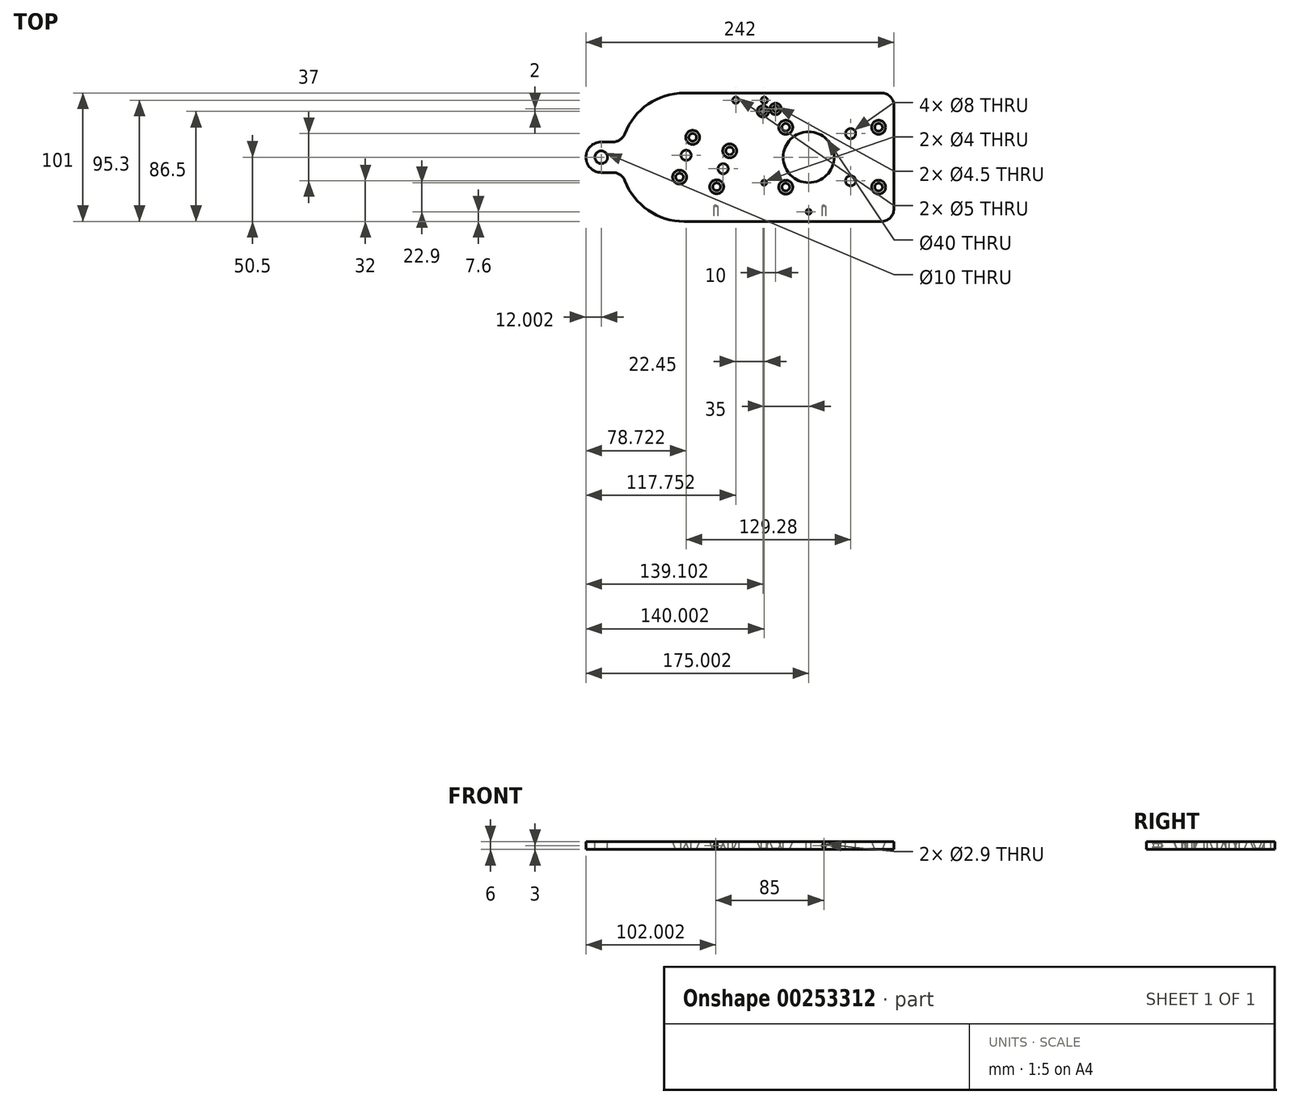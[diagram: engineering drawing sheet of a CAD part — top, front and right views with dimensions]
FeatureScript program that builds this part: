
annotation { "Feature Type Name" : "Feature", "Feature Type Description" : "" }
export const myFeature = defineFeature(function(context is Context, id is Id, definition is map)
    precondition{}
    {
        {
            var Q0;
            Q0=qCreatedBy(makeId("Top.planeOp"),FACE);
            var sketch = newSketch(context, id + "F0", { "sketchPlane" : qUnion([Q0])});
            skLineSegment(sketch, "E0.bottom", {"start": v(82.4, 50.5) * mm, "end": v(-82.4, 50.5) * mm});
            skLineSegment(sketch, "E0.top", {"start": v(82.4, -50.5) * mm, "end": v(-82.4, -50.5) * mm});
            skLineSegment(sketch, "E0.left", {"start": v(82.4, 50.5) * mm, "end": v(82.4, -50.5) * mm});
            skPoint(sketch, "E0.middle", {"position": v(0, 0) * mm});
            skLineSegment(sketch, "E1", {"start": v(-138.4, 12) * mm, "end": v(-147.6, 12) * mm});
            skLineSegment(sketch, "E2", {"start": v(-147.6, -12) * mm, "end": v(-138.4, -12) * mm});
            skCircle(sketch, "E3", {"center": v(-147.6, 0) * mm, "radius": 5 * mm});
            skCircle(sketch, "E4", {"center": v(15.4, 0) * mm, "radius": 20 * mm});
            skCircle(sketch, "E5", {"center": v(-80.89, 1.52) * mm, "radius": 4 * mm});
            skCircle(sketch, "E6", {"center": v(-51.76, -9.1) * mm, "radius": 4 * mm});
            skCircle(sketch, "E7", {"center": v(48.4, 18.5) * mm, "radius": 4 * mm});
            skCircle(sketch, "E8", {"center": v(48.4, -18.5) * mm, "radius": 4 * mm});
            skArc(sketch, "E9", {"start": v(-147.6, 12) * mm, "mid": v(-159.6, 0) * mm, "end": v(-147.6, -12) * mm});
            skArc(sketch, "E10", {"start": v(-138.4, 12) * mm, "mid": v(-132.74, 13.76) * mm, "end": v(-129.07, 18.42) * mm});
            skArc(sketch, "E11", {"start": v(-129.07, 18.42) * mm, "mid": v(-110.71, 41.7) * mm, "end": v(-82.4, 50.5) * mm});
            skArc(sketch, "E12.MirrorCS", {"start": v(-129.07, -18.42) * mm, "mid": v(-110.71, -41.7) * mm, "end": v(-82.4, -50.5) * mm});
            skArc(sketch, "E13.MirrorCS", {"start": v(-138.4, -12) * mm, "mid": v(-132.74, -13.76) * mm, "end": v(-129.07, -18.42) * mm});
            skCircle(sketch, "E14", {"center": v(15.4, -42.9) * mm, "radius": 2 * mm});
            skCircle(sketch, "E15", {"center": v(-19.6, -20) * mm, "radius": 2 * mm});
            skPoint(sketch, "E16", {"position": v(-86.02, -15.6) * mm});
            skPoint(sketch, "E17", {"position": v(-75.76, 15.6) * mm});
            skPoint(sketch, "E18", {"position": v(-56.89, -23.2) * mm});
            skPoint(sketch, "E19", {"position": v(-46.63, 5) * mm});
            skPoint(sketch, "E20", {"position": v(-2.6, -23.5) * mm});
            skPoint(sketch, "E21", {"position": v(-20.5, 36) * mm});
            skPoint(sketch, "E22", {"position": v(-10.5, 38) * mm});
            skPoint(sketch, "E23", {"position": v(-2.6, 23.5) * mm});
            skPoint(sketch, "E24", {"position": v(70.4, 23.5) * mm});
            skPoint(sketch, "E25", {"position": v(70.4, -23.5) * mm});
            skPoint(sketch, "E26", {"position": v(-41.86, 44.8) * mm});
            skPoint(sketch, "E27", {"position": v(-19.4, 44.8) * mm});
            skSolve(sketch);
        }
        {
            var Q0;
            Q0=makeQuery(id+"F0.imprint","IMPRINT",FACE,{"disambiguationData":[TD([[makeQuery(id+"F0.imprint","IMPRINT",EDGE,{"derivedFrom":sQuery(id+"F0.wireOp",EDGE,"E0.bottom")}),1.0]])]});
            extrude(context, id + "F1", {"entities" : qUnion([Q0]), "oppositeDirection" : true, "depth" : 6 * mm});
        }
        {
            var Q0;
            Q0=sQuery(id+"F0.wireOp",VERTEX,"E16");
            var Q1;
            Q1=sQuery(id+"F0.wireOp",VERTEX,"E17");
            var Q2;
            Q2=sQuery(id+"F0.wireOp",VERTEX,"E19");
            var Q3;
            Q3=sQuery(id+"F0.wireOp",VERTEX,"E18");
            var Q4;
            Q4=sQuery(id+"F0.wireOp",VERTEX,"E20");
            var Q5;
            Q5=sQuery(id+"F0.wireOp",VERTEX,"E23");
            var Q6;
            Q6=sQuery(id+"F0.wireOp",VERTEX,"E25");
            var Q7;
            Q7=sQuery(id+"F0.wireOp",VERTEX,"E24");
            var Q8;
            Q8=makeQuery(id+"F1.opExtrude","SWEPT_BODY",BODY,{"disambiguationData":[OSD([sQuery(id+"F0.wireOp",EDGE,"E0.bottom"),sQuery(id+"F0.wireOp",EDGE,"E0.top"),sQuery(id+"F0.wireOp",EDGE,"E0.left"),sQuery(id+"F0.wireOp",EDGE,"E1"),sQuery(id+"F0.wireOp",EDGE,"E2"),sQuery(id+"F0.wireOp",EDGE,"E3"),sQuery(id+"F0.wireOp",EDGE,"E4"),sQuery(id+"F0.wireOp",EDGE,"E5"),sQuery(id+"F0.wireOp",EDGE,"E6"),sQuery(id+"F0.wireOp",EDGE,"E7"),sQuery(id+"F0.wireOp",EDGE,"E8"),sQuery(id+"F0.wireOp",EDGE,"E9"),sQuery(id+"F0.wireOp",EDGE,"E10"),sQuery(id+"F0.wireOp",EDGE,"E11"),sQuery(id+"F0.wireOp",EDGE,"E12.MirrorCS"),sQuery(id+"F0.wireOp",EDGE,"E13.MirrorCS"),sQuery(id+"F0.wireOp",EDGE,"E14"),sQuery(id+"F0.wireOp",EDGE,"E15")])]});
            hole(context, id + "F2", {"style" : HoleStyle.C_SINK, "endStyle" : HoleEndStyle.THROUGH, "holeDiameter" : 5.5 * mm, "cSinkDiameter" : 11 * mm, "cSinkAngle" : 45 * degree, "tappedDepth" : 12 * mm, "tapClearance" : 3, "locations" : qUnion([Q0, Q1, Q2, Q3, Q4, Q5, Q6, Q7]), "scope" : qUnion([Q8])});
        }
        {
            var Q0;
            Q0=sQuery(id+"F0.wireOp",VERTEX,"E21");
            var Q1;
            Q1=sQuery(id+"F0.wireOp",VERTEX,"E22");
            var Q2;
            Q2=makeQuery(id+"F1.opExtrude","SWEPT_BODY",BODY,{"disambiguationData":[OSD([sQuery(id+"F0.wireOp",EDGE,"E0.bottom"),sQuery(id+"F0.wireOp",EDGE,"E0.top"),sQuery(id+"F0.wireOp",EDGE,"E0.left"),sQuery(id+"F0.wireOp",EDGE,"E1"),sQuery(id+"F0.wireOp",EDGE,"E2"),sQuery(id+"F0.wireOp",EDGE,"E3"),sQuery(id+"F0.wireOp",EDGE,"E4"),sQuery(id+"F0.wireOp",EDGE,"E5"),sQuery(id+"F0.wireOp",EDGE,"E6"),sQuery(id+"F0.wireOp",EDGE,"E7"),sQuery(id+"F0.wireOp",EDGE,"E8"),sQuery(id+"F0.wireOp",EDGE,"E9"),sQuery(id+"F0.wireOp",EDGE,"E10"),sQuery(id+"F0.wireOp",EDGE,"E11"),sQuery(id+"F0.wireOp",EDGE,"E12.MirrorCS"),sQuery(id+"F0.wireOp",EDGE,"E13.MirrorCS"),sQuery(id+"F0.wireOp",EDGE,"E14"),sQuery(id+"F0.wireOp",EDGE,"E15")])]});
            hole(context, id + "F3", {"style" : HoleStyle.C_SINK, "endStyle" : HoleEndStyle.THROUGH, "holeDiameter" : 4.5 * mm, "cSinkDiameter" : 9 * mm, "cSinkAngle" : 45 * degree, "tappedDepth" : 12 * mm, "tapClearance" : 3, "locations" : qUnion([Q0, Q1]), "scope" : qUnion([Q2])});
        }
        {
            var Q0;
            Q0=sQuery(id+"F0.wireOp",VERTEX,"E26");
            var Q1;
            Q1=sQuery(id+"F0.wireOp",VERTEX,"E27");
            var Q2;
            Q2=makeQuery(id+"F1.opExtrude","SWEPT_BODY",BODY,{"disambiguationData":[OSD([sQuery(id+"F0.wireOp",EDGE,"E0.bottom"),sQuery(id+"F0.wireOp",EDGE,"E0.top"),sQuery(id+"F0.wireOp",EDGE,"E0.left"),sQuery(id+"F0.wireOp",EDGE,"E1"),sQuery(id+"F0.wireOp",EDGE,"E2"),sQuery(id+"F0.wireOp",EDGE,"E3"),sQuery(id+"F0.wireOp",EDGE,"E4"),sQuery(id+"F0.wireOp",EDGE,"E5"),sQuery(id+"F0.wireOp",EDGE,"E6"),sQuery(id+"F0.wireOp",EDGE,"E7"),sQuery(id+"F0.wireOp",EDGE,"E8"),sQuery(id+"F0.wireOp",EDGE,"E9"),sQuery(id+"F0.wireOp",EDGE,"E10"),sQuery(id+"F0.wireOp",EDGE,"E11"),sQuery(id+"F0.wireOp",EDGE,"E12.MirrorCS"),sQuery(id+"F0.wireOp",EDGE,"E13.MirrorCS"),sQuery(id+"F0.wireOp",EDGE,"E14"),sQuery(id+"F0.wireOp",EDGE,"E15")])]});
            hole(context, id + "F4", {"style" : HoleStyle.SIMPLE, "endStyle" : HoleEndStyle.THROUGH, "standardTappedOrClearance" : lookupTablePath({ "standard" : "ISO", "size" : "5", "type" : "Drilled" }), "standardBlindInLast" : lookupTablePath({ "standard" : "ISO", "size" : "5", "type" : "Drilled" }), "holeDiameter" : 5 * mm, "tappedDepth" : 12 * mm, "tapClearance" : 3, "locations" : qUnion([Q0, Q1]), "scope" : qUnion([Q2])});
        }
        {
            var Q0;
            Q0=makeQuery(id+"F1.opExtrude","SWEPT_FACE",FACE,{"disambiguationData":[OSD([sQuery(id+"F0.wireOp",EDGE,"E0.top")])]});
            var sketch = newSketch(context, id + "F5", { "sketchPlane" : qUnion([Q0])});
            skPoint(sketch, "E28", {"position": v(-57.6, -3) * mm});
            skPoint(sketch, "E29", {"position": v(27.4, -3) * mm});
            skSolve(sketch);
        }
        {
            var Q0;
            Q0=sQuery(id+"F5.wireOp",VERTEX,"E28");
            var Q1;
            Q1=sQuery(id+"F5.wireOp",VERTEX,"E29");
            var Q2;
            Q2=makeQuery(id+"F1.opExtrude","SWEPT_BODY",BODY,{"disambiguationData":[OSD([sQuery(id+"F0.wireOp",EDGE,"E0.bottom"),sQuery(id+"F0.wireOp",EDGE,"E0.top"),sQuery(id+"F0.wireOp",EDGE,"E0.left"),sQuery(id+"F0.wireOp",EDGE,"E1"),sQuery(id+"F0.wireOp",EDGE,"E2"),sQuery(id+"F0.wireOp",EDGE,"E3"),sQuery(id+"F0.wireOp",EDGE,"E4"),sQuery(id+"F0.wireOp",EDGE,"E5"),sQuery(id+"F0.wireOp",EDGE,"E6"),sQuery(id+"F0.wireOp",EDGE,"E7"),sQuery(id+"F0.wireOp",EDGE,"E8"),sQuery(id+"F0.wireOp",EDGE,"E9"),sQuery(id+"F0.wireOp",EDGE,"E10"),sQuery(id+"F0.wireOp",EDGE,"E11"),sQuery(id+"F0.wireOp",EDGE,"E12.MirrorCS"),sQuery(id+"F0.wireOp",EDGE,"E13.MirrorCS"),sQuery(id+"F0.wireOp",EDGE,"E14"),sQuery(id+"F0.wireOp",EDGE,"E15")])]});
            hole(context, id + "F6", {"style" : HoleStyle.SIMPLE, "endStyle" : HoleEndStyle.BLIND, "holeDiameter" : 2.9 * mm, "holeDepth" : 12 * mm, "tappedDepth" : 12 * mm, "tapClearance" : 3, "locations" : qUnion([Q0, Q1]), "scope" : qUnion([Q2])});
        }
        {
            var Q0;
            Q0=makeQuery(id+"F1.opExtrude","SWEPT_EDGE",EDGE,{"disambiguationData":[OSD([sQuery(id+"F0.wireOp",EDGE,"E0.top"),sQuery(id+"F0.wireOp",EDGE,"E0.left")])]});
            var Q1;
            Q1=makeQuery(id+"F1.opExtrude","SWEPT_EDGE",EDGE,{"disambiguationData":[OSD([sQuery(id+"F0.wireOp",EDGE,"E0.bottom"),sQuery(id+"F0.wireOp",EDGE,"E0.left")])]});
            fillet(context, id + "F7", {"entities" : qUnion([Q0, Q1]), "radius" : 10 * mm, "tangentPropagation" : true, "allowEdgeOverflow" : false});
        }
    });
